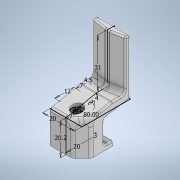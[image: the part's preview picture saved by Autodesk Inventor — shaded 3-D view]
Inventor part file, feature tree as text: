
AUTODESK INVENTOR PART (.ipt)
format: ipt  version: 2020.2 (Build 242310000, 310)  size: 353,792 bytes
history: native  units: mm
features: chamfer x4, extrude x3, fillet x3, sketch x2, hole x1
ambient origin geometry x8: Origin, YZ Plane, XZ Plane, XY Plane, X Axis, Y Axis, Z Axis, Center Point
bodies: Solid2 (feature_tree)
feature tree (13):
  sketch  "Sketch1"  dims[d0=20.0mm d1=7.0mm]
  sketch  "Sketch2"  dims[d2=3.5mm d3=7.0mm d4=12.0mm d9=20.2mm d10=20.0mm d11=0.0mm d12=3.5mm d13=6.0mm d14=7.0mm d15=16.0mm d16=90.0deg d17=8.0mm d18=20.594885mm d19=1.0mm d20=6.0mm d21=2.0mm d22=45.0deg d23=3.0mm d24=2.0mm d25=60.0deg d26=31.0mm d27=4.0mm d28=4.5mm d29=7.0mm d30=3.0mm d31=1.5mm d32=2.0mm d33=13.962634mm d34=1.5mm d35=2.0mm d36=13.962634mm d37=2.0mm d42=1.0mm d43=34.0mm d44=0.0mm d46=3.0mm d47=13.962634mm d48=20.0mm d50=2.0mm d51=0.0mm d52=1.0mm d53=0.872665mm]
  extrude  "Extrusion3"  Depth=7.0mm
  hole  "Hole1"  [1 undecoded]
  extrude  "Extrusion4"  Depth=1.0mm
  fillet  "Fillet1"  Radius=20.2mm
  chamfer  "Chamfer1"  Distance=20.0mm
  chamfer  "Chamfer2"  Distance=3.5mm
  chamfer  "Chamfer3"  Distance=6.0mm
  chamfer  "Chamfer4"  Distance=16.0mm Angle=90.0deg
  extrude  "Extrusion5"  Depth=1.0mm
  fillet  "Fillet2"  Radius=6.0mm
  fillet  "Fillet3"  Radius=3.0mm
note: 1 required parameter value undecoded (feature->parameter linkage not recoverable at this tier; creation-order binding heuristic only, values carry confidence <= 0.55)
